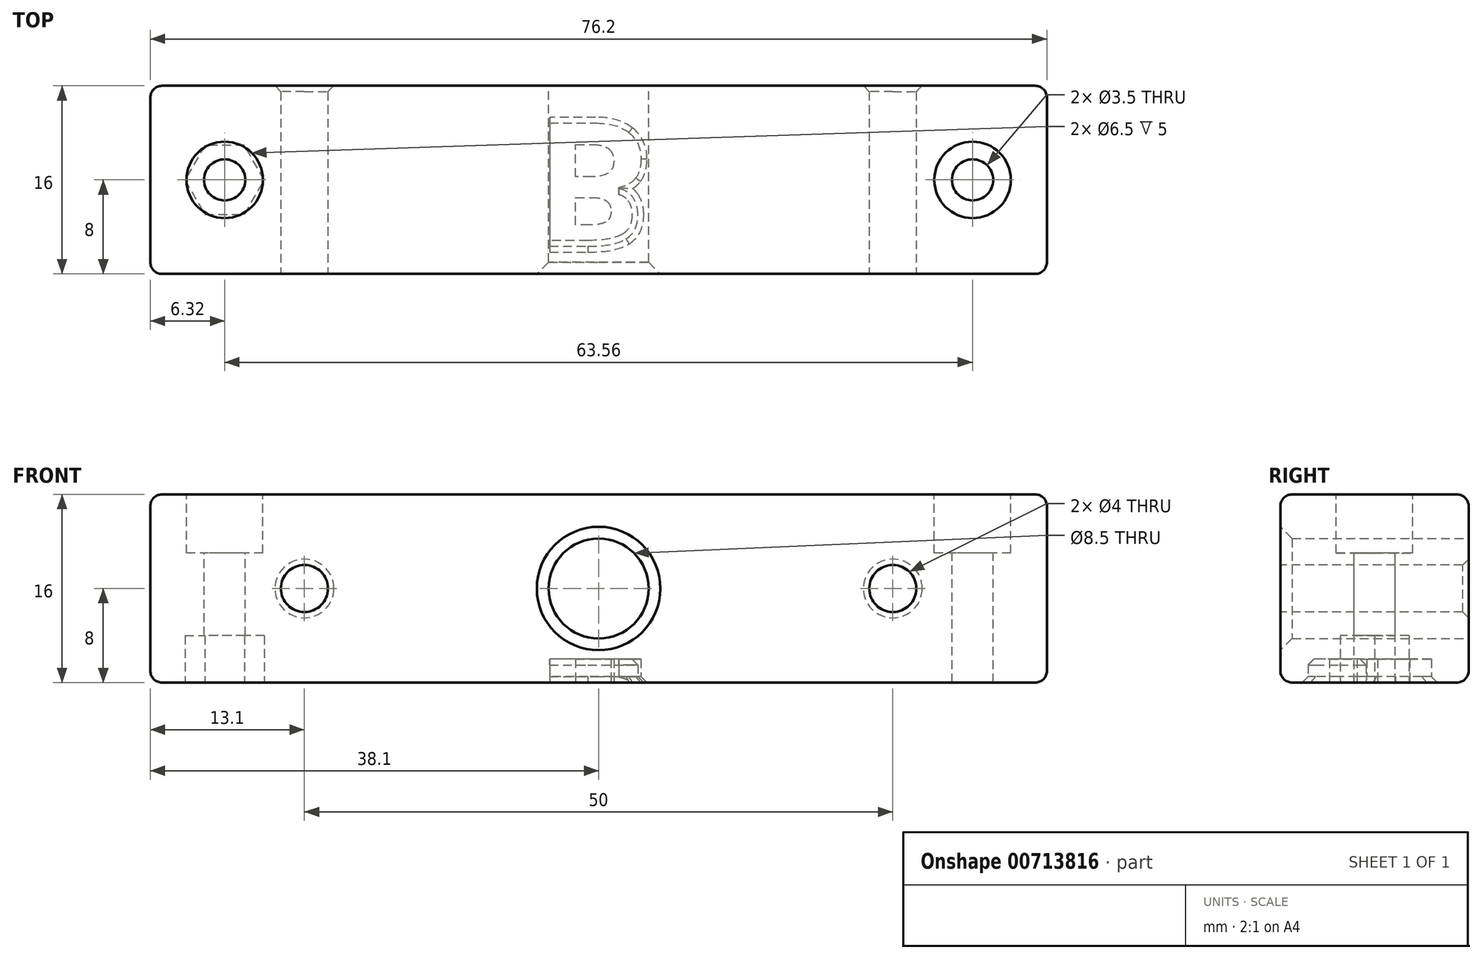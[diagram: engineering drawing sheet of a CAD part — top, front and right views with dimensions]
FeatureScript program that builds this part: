
annotation { "Feature Type Name" : "Feature", "Feature Type Description" : "" }
export const myFeature = defineFeature(function(context is Context, id is Id, definition is map)
    precondition{}
    {
        {
            var Q0;
            Q0=qCreatedBy(makeId("Top.planeOp"),FACE);
            var sketch = newSketch(context, id + "F0", { "sketchPlane" : qUnion([Q0])});
            skLineSegment(sketch, "E0.bottom", {"start": v(-38.1, -8) * mm, "end": v(38.1, -8) * mm});
            skLineSegment(sketch, "E0.top", {"start": v(-38.1, 8) * mm, "end": v(38.1, 8) * mm});
            skLineSegment(sketch, "E0.left", {"start": v(-38.1, -8) * mm, "end": v(-38.1, 8) * mm});
            skLineSegment(sketch, "E0.right", {"start": v(38.1, -8) * mm, "end": v(38.1, 8) * mm});
            skPoint(sketch, "E0.middle", {"position": v(0, 0) * mm});
            skSolve(sketch);
        }
        {
            var Q0;
            Q0=makeQuery(id+"F0.imprint","IMPRINT",FACE,{"disambiguationData":[TD([[makeQuery(id+"F0.imprint","IMPRINT",EDGE,{"derivedFrom":sQuery(id+"F0.wireOp",EDGE,"E0.bottom")}),1.0]])]});
            extrude(context, id + "F1", {"entities" : qUnion([Q0]), "depth" : 16 * mm, "offsetDistance" : 25 * mm});
        }
        {
            var Q0;
            Q0=makeQuery(id+"F1.opExtrude","CAP_FACE",FACE,{"disambiguationData":[OSD([sQuery(id+"F0.wireOp",EDGE,"E0.bottom"),sQuery(id+"F0.wireOp",EDGE,"E0.top"),sQuery(id+"F0.wireOp",EDGE,"E0.left"),sQuery(id+"F0.wireOp",EDGE,"E0.right")])],"isStart":false});
            var sketch = newSketch(context, id + "F2", { "sketchPlane" : qUnion([Q0])});
            skPoint(sketch, "E1", {"position": v(-31.78, 0) * mm});
            skPoint(sketch, "E2", {"position": v(31.78, 0) * mm});
            skSolve(sketch);
        }
        {
            var Q0;
            Q0=sQuery(id+"F2.wireOp",VERTEX,"E2");
            var Q1;
            Q1=sQuery(id+"F2.wireOp",VERTEX,"E1");
            var Q2;
            Q2=makeQuery(id+"F1.opExtrude","SWEPT_BODY",BODY,{"disambiguationData":[OSD([sQuery(id+"F0.wireOp",EDGE,"E0.bottom"),sQuery(id+"F0.wireOp",EDGE,"E0.top"),sQuery(id+"F0.wireOp",EDGE,"E0.left"),sQuery(id+"F0.wireOp",EDGE,"E0.right")])]});
            hole(context, id + "F3", {"style" : HoleStyle.C_BORE, "endStyle" : HoleEndStyle.THROUGH, "holeDiameter" : 3.5 * mm, "cBoreDiameter" : 6.5 * mm, "cBoreDepth" : 5 * mm, "majorDiameter" : 5 * mm, "isTappedThrough" : true, "tappedDepth" : 12 * mm, "tapClearance" : 3, "locations" : qUnion([Q0, Q1]), "scope" : qUnion([Q2])});
        }
        {
            var Q0;
            Q0=makeQuery(id+"F1.opExtrude","CAP_FACE",FACE,{"disambiguationData":[OSD([sQuery(id+"F0.wireOp",EDGE,"E0.bottom"),sQuery(id+"F0.wireOp",EDGE,"E0.top"),sQuery(id+"F0.wireOp",EDGE,"E0.left"),sQuery(id+"F0.wireOp",EDGE,"E0.right")])],"isStart":true});
            var sketch = newSketch(context, id + "F4", { "sketchPlane" : qUnion([Q0])});
            skCircle(sketch, "E3.cCircle", {"center": v(-31.78, 0) * mm, "radius": 3.38 * mm, "construction": true});
            skPoint(sketch, "E3.cCircle.perimeterSnap0", {"position": v(-38.1, 0) * mm});
            skLineSegment(sketch, "E3.0", {"start": v(-35.16, 0) * mm, "end": v(-33.47, 2.93) * mm});
            skPoint(sketch, "E3.0.startSnap0", {"position": v(-38.1, 0) * mm});
            skLineSegment(sketch, "E3.1", {"start": v(-33.47, 2.93) * mm, "end": v(-30.1, 2.93) * mm});
            skLineSegment(sketch, "E3.2", {"start": v(-30.1, 2.93) * mm, "end": v(-28.4, 0) * mm});
            skLineSegment(sketch, "E3.3", {"start": v(-28.4, 0) * mm, "end": v(-30.1, -2.92) * mm});
            skLineSegment(sketch, "E3.4", {"start": v(-30.1, -2.92) * mm, "end": v(-33.47, -2.92) * mm});
            skLineSegment(sketch, "E3.5", {"start": v(-33.47, -2.93) * mm, "end": v(-35.16, 0) * mm});
            skSolve(sketch);
        }
        {
            var Q0;
            Q0=makeQuery(id+"F4.imprint","IMPRINT",FACE,{"disambiguationData":[TD([[makeQuery(id+"F4.imprint","IMPRINT",EDGE,{"derivedFrom":sQuery(id+"F4.wireOp",EDGE,"E3.0")}),-1.0]])]});
            extrude(context, id + "F5", {"entities" : qUnion([Q0]), "operationType" : NewBodyOperationType.REMOVE, "oppositeDirection" : true, "depth" : 4 * mm, "offsetDistance" : 25 * mm});
        }
        {
            var Q0;
            Q0=makeQuery(id+"F1.opExtrude","SWEPT_FACE",FACE,{"disambiguationData":[OSD([sQuery(id+"F0.wireOp",EDGE,"E0.top")])]});
            var sketch = newSketch(context, id + "F6", { "sketchPlane" : qUnion([Q0])});
            skCircle(sketch, "E4", {"center": v(0, 8) * mm, "radius": 4.25 * mm});
            skSolve(sketch);
        }
        {
            var Q0;
            Q0=makeQuery(id+"F6.imprint","IMPRINT",FACE,{"disambiguationData":[TD([[makeQuery(id+"F6.imprint","IMPRINT",EDGE,{"derivedFrom":sQuery(id+"F6.wireOp",EDGE,"E4")}),1.0]])]});
            extrude(context, id + "F7", {"entities" : qUnion([Q0]), "operationType" : NewBodyOperationType.REMOVE, "endBound" : BoundingType.THROUGH_ALL, "oppositeDirection" : true, "depth" : 12 * mm, "offsetDistance" : 25 * mm});
        }
        {
            var Q0;
            Q0=makeQuery(id+"F1.opExtrude","CAP_FACE",FACE,{"disambiguationData":[OSD([sQuery(id+"F0.wireOp",EDGE,"E0.bottom"),sQuery(id+"F0.wireOp",EDGE,"E0.top"),sQuery(id+"F0.wireOp",EDGE,"E0.left"),sQuery(id+"F0.wireOp",EDGE,"E0.right")])],"isStart":true});
            var sketch = newSketch(context, id + "F8", { "sketchPlane" : qUnion([Q0])});
            skText(sketch, "E5", { "text": "B", "fontName": "OpenSans-Bold.ttf"});
            const initialGuessF8  = {"E5": [-0.00549, -0.00483, 1, 0, 0.01057]};
            skSetInitialGuess(sketch, initialGuessF8);
            skSolve(sketch);
        }
        {
            var Q0;
            Q0=qSketchRegion(id+"F8",true);
            extrude(context, id + "F9", {"entities" : qUnion([Q0]), "operationType" : NewBodyOperationType.REMOVE, "oppositeDirection" : true, "depth" : 2 * mm, "offsetDistance" : 25 * mm});
        }
        {
            var Q0;
            Q0=makeQuery(id+"F9.boolean.opBoolean","COPY",EDGE,{"derivedFrom":makeQuery(id+"F9.opExtrude","CAP_EDGE",EDGE,{"disambiguationData":[OSD([sQuery(id+"F8.wireOp",EDGE,"E5.sketch_text.stroke-1")])],"isStart":true})});
            var Q1;
            Q1=makeQuery(id+"F9.boolean.opBoolean","COPY",EDGE,{"derivedFrom":makeQuery(id+"F9.opExtrude","CAP_EDGE",EDGE,{"disambiguationData":[OSD([sQuery(id+"F8.wireOp",EDGE,"E5.sketch_text.stroke-0")])],"isStart":true})});
            var Q2;
            Q2=makeQuery(id+"F9.boolean.opBoolean","COPY",EDGE,{"derivedFrom":makeQuery(id+"F9.opExtrude","CAP_EDGE",EDGE,{"disambiguationData":[OSD([sQuery(id+"F8.wireOp",EDGE,"E5.sketch_text.stroke-7")])],"isStart":true})});
            var Q3;
            Q3=makeQuery(id+"F9.boolean.opBoolean","COPY",EDGE,{"derivedFrom":makeQuery(id+"F9.opExtrude","CAP_EDGE",EDGE,{"disambiguationData":[OSD([sQuery(id+"F8.wireOp",EDGE,"E5.sketch_text.stroke-6")])],"isStart":true})});
            var Q4;
            Q4=makeQuery(id+"F9.boolean.opBoolean","COPY",EDGE,{"derivedFrom":makeQuery(id+"F9.opExtrude","CAP_EDGE",EDGE,{"disambiguationData":[OSD([sQuery(id+"F8.wireOp",EDGE,"E5.sketch_text.stroke-5")])],"isStart":true})});
            var Q5;
            Q5=makeQuery(id+"F9.boolean.opBoolean","COPY",EDGE,{"derivedFrom":makeQuery(id+"F9.opExtrude","CAP_EDGE",EDGE,{"disambiguationData":[OSD([sQuery(id+"F8.wireOp",EDGE,"E5.sketch_text.stroke-4")])],"isStart":false})});
            var Q6;
            Q6=makeQuery(id+"F9.boolean.opBoolean","COPY",EDGE,{"derivedFrom":makeQuery(id+"F9.opExtrude","CAP_EDGE",EDGE,{"disambiguationData":[OSD([sQuery(id+"F8.wireOp",EDGE,"E5.sketch_text.stroke-2")])],"isStart":true})});
            var Q7;
            Q7=makeQuery(id+"F9.boolean.opBoolean","COPY",EDGE,{"derivedFrom":makeQuery(id+"F9.opExtrude","CAP_EDGE",EDGE,{"disambiguationData":[OSD([sQuery(id+"F8.wireOp",EDGE,"E5.sketch_text.stroke-3")])],"isStart":true})});
            chamfer(context, id + "F10", {"entities" : qUnion([Q0, Q1, Q2, Q3, Q4, Q5, Q6, Q7]), "width" : 0.5 * mm, "tangentPropagation" : true});
        }
        {
            var Q0;
            Q0=makeQuery(id+"F7.boolean.opBoolean","COPY",EDGE,{"derivedFrom":makeQuery(id+"F7.opExtrude","CAP_EDGE",EDGE,{"disambiguationData":[OSD([sQuery(id+"F6.wireOp",EDGE,"E4")])],"isStart":true})});
            var Q1;
            Q1=makeQuery(id+"F7.boolean.opBoolean","INTERSECT",EDGE,{"derivedFrom":[makeQuery(id+"F1.opExtrude","SWEPT_FACE",FACE,{"disambiguationData":[OSD([sQuery(id+"F0.wireOp",EDGE,"E0.bottom")])]}),makeQuery(id+"F7.opExtrude","SWEPT_FACE",FACE,{"disambiguationData":[OSD([sQuery(id+"F6.wireOp",EDGE,"E4")])]})]});
            chamfer(context, id + "F11", {"entities" : qUnion([Q0, Q1]), "width" : 1 * mm, "tangentPropagation" : true});
        }
        {
            var Q0;
            Q0=makeQuery(id+"F1.opExtrude","SWEPT_EDGE",EDGE,{"disambiguationData":[OSD([sQuery(id+"F0.wireOp",EDGE,"E0.top"),sQuery(id+"F0.wireOp",EDGE,"E0.right")])]});
            var Q1;
            Q1=makeQuery(id+"F1.opExtrude","CAP_EDGE",EDGE,{"disambiguationData":[OSD([sQuery(id+"F0.wireOp",EDGE,"E0.top")])],"isStart":true});
            var Q2;
            Q2=makeQuery(id+"F1.opExtrude","CAP_EDGE",EDGE,{"disambiguationData":[OSD([sQuery(id+"F0.wireOp",EDGE,"E0.top")])],"isStart":false});
            var Q3;
            Q3=makeQuery(id+"F1.opExtrude","SWEPT_EDGE",EDGE,{"disambiguationData":[OSD([sQuery(id+"F0.wireOp",EDGE,"E0.top"),sQuery(id+"F0.wireOp",EDGE,"E0.left")])]});
            var Q4;
            Q4=makeQuery(id+"F1.opExtrude","SWEPT_EDGE",EDGE,{"disambiguationData":[OSD([sQuery(id+"F0.wireOp",EDGE,"E0.bottom"),sQuery(id+"F0.wireOp",EDGE,"E0.right")])]});
            var Q5;
            Q5=makeQuery(id+"F1.opExtrude","CAP_EDGE",EDGE,{"disambiguationData":[OSD([sQuery(id+"F0.wireOp",EDGE,"E0.right")])],"isStart":false});
            var Q6;
            Q6=makeQuery(id+"F1.opExtrude","CAP_EDGE",EDGE,{"disambiguationData":[OSD([sQuery(id+"F0.wireOp",EDGE,"E0.right")])],"isStart":true});
            var Q7;
            Q7=makeQuery(id+"F1.opExtrude","CAP_EDGE",EDGE,{"disambiguationData":[OSD([sQuery(id+"F0.wireOp",EDGE,"E0.bottom")])],"isStart":false});
            var Q8;
            Q8=makeQuery(id+"F1.opExtrude","CAP_EDGE",EDGE,{"disambiguationData":[OSD([sQuery(id+"F0.wireOp",EDGE,"E0.left")])],"isStart":false});
            var Q9;
            Q9=makeQuery(id+"F1.opExtrude","SWEPT_EDGE",EDGE,{"disambiguationData":[OSD([sQuery(id+"F0.wireOp",EDGE,"E0.bottom"),sQuery(id+"F0.wireOp",EDGE,"E0.left")])]});
            var Q10;
            Q10=makeQuery(id+"F1.opExtrude","CAP_EDGE",EDGE,{"disambiguationData":[OSD([sQuery(id+"F0.wireOp",EDGE,"E0.bottom")])],"isStart":true});
            var Q11;
            Q11=makeQuery(id+"F1.opExtrude","CAP_EDGE",EDGE,{"disambiguationData":[OSD([sQuery(id+"F0.wireOp",EDGE,"E0.left")])],"isStart":true});
            fillet(context, id + "F12", {"entities" : qUnion([Q0, Q1, Q2, Q3, Q4, Q5, Q6, Q7, Q8, Q9, Q10, Q11]), "radius" : 1 * mm, "tangentPropagation" : true, "allowEdgeOverflow" : false});
        }
        {
            var Q0;
            Q0=makeQuery(id+"F1.opExtrude","SWEPT_FACE",FACE,{"disambiguationData":[OSD([sQuery(id+"F0.wireOp",EDGE,"E0.bottom")])]});
            var sketch = newSketch(context, id + "F13", { "sketchPlane" : qUnion([Q0])});
            skPoint(sketch, "E6", {"position": v(25, 8) * mm});
            skPoint(sketch, "E7", {"position": v(-25, 8) * mm});
            skCircle(sketch, "E8", {"center": v(-25, 8) * mm, "radius": 2 * mm});
            skCircle(sketch, "E9", {"center": v(25, 8) * mm, "radius": 2 * mm});
            skSolve(sketch);
        }
        {
            var Q0;
            Q0=makeQuery(id+"F13.imprint","IMPRINT",FACE,{"disambiguationData":[TD([[makeQuery(id+"F13.imprint","IMPRINT",EDGE,{"derivedFrom":sQuery(id+"F13.wireOp",EDGE,"E8")}),1.0]])]});
            var Q1;
            Q1=makeQuery(id+"F13.imprint","IMPRINT",FACE,{"disambiguationData":[TD([[makeQuery(id+"F13.imprint","IMPRINT",EDGE,{"derivedFrom":sQuery(id+"F13.wireOp",EDGE,"E9")}),1.0]])]});
            extrude(context, id + "F14", {"entities" : qUnion([Q0, Q1]), "operationType" : NewBodyOperationType.REMOVE, "endBound" : BoundingType.THROUGH_ALL, "oppositeDirection" : true, "depth" : 25 * mm, "offsetDistance" : 25 * mm});
        }
        {
            var Q0;
            Q0=makeQuery(id+"F14.boolean.opBoolean","COPY",EDGE,{"derivedFrom":makeQuery(id+"F14.opExtrude","CAP_EDGE",EDGE,{"disambiguationData":[OSD([sQuery(id+"F13.wireOp",EDGE,"E8")])],"isStart":true})});
            var Q1;
            Q1=makeQuery(id+"F14.boolean.opBoolean","COPY",EDGE,{"derivedFrom":makeQuery(id+"F14.opExtrude","CAP_EDGE",EDGE,{"disambiguationData":[OSD([sQuery(id+"F13.wireOp",EDGE,"E9")])],"isStart":true})});
            var Q2;
            Q2=makeQuery(id+"F14.boolean.opBoolean","INTERSECT",EDGE,{"derivedFrom":[makeQuery(id+"F1.opExtrude","SWEPT_FACE",FACE,{"disambiguationData":[OSD([sQuery(id+"F0.wireOp",EDGE,"E0.top")])]}),makeQuery(id+"F14.opExtrude","SWEPT_FACE",FACE,{"disambiguationData":[OSD([sQuery(id+"F13.wireOp",EDGE,"E9")])]})]});
            var Q3;
            Q3=makeQuery(id+"F14.boolean.opBoolean","INTERSECT",EDGE,{"derivedFrom":[makeQuery(id+"F1.opExtrude","SWEPT_FACE",FACE,{"disambiguationData":[OSD([sQuery(id+"F0.wireOp",EDGE,"E0.top")])]}),makeQuery(id+"F14.opExtrude","SWEPT_FACE",FACE,{"disambiguationData":[OSD([sQuery(id+"F13.wireOp",EDGE,"E8")])]})]});
            chamfer(context, id + "F15", {"entities" : qUnion([Q0, Q1, Q2, Q3]), "width" : 0.5 * mm, "tangentPropagation" : true});
        }
    });
